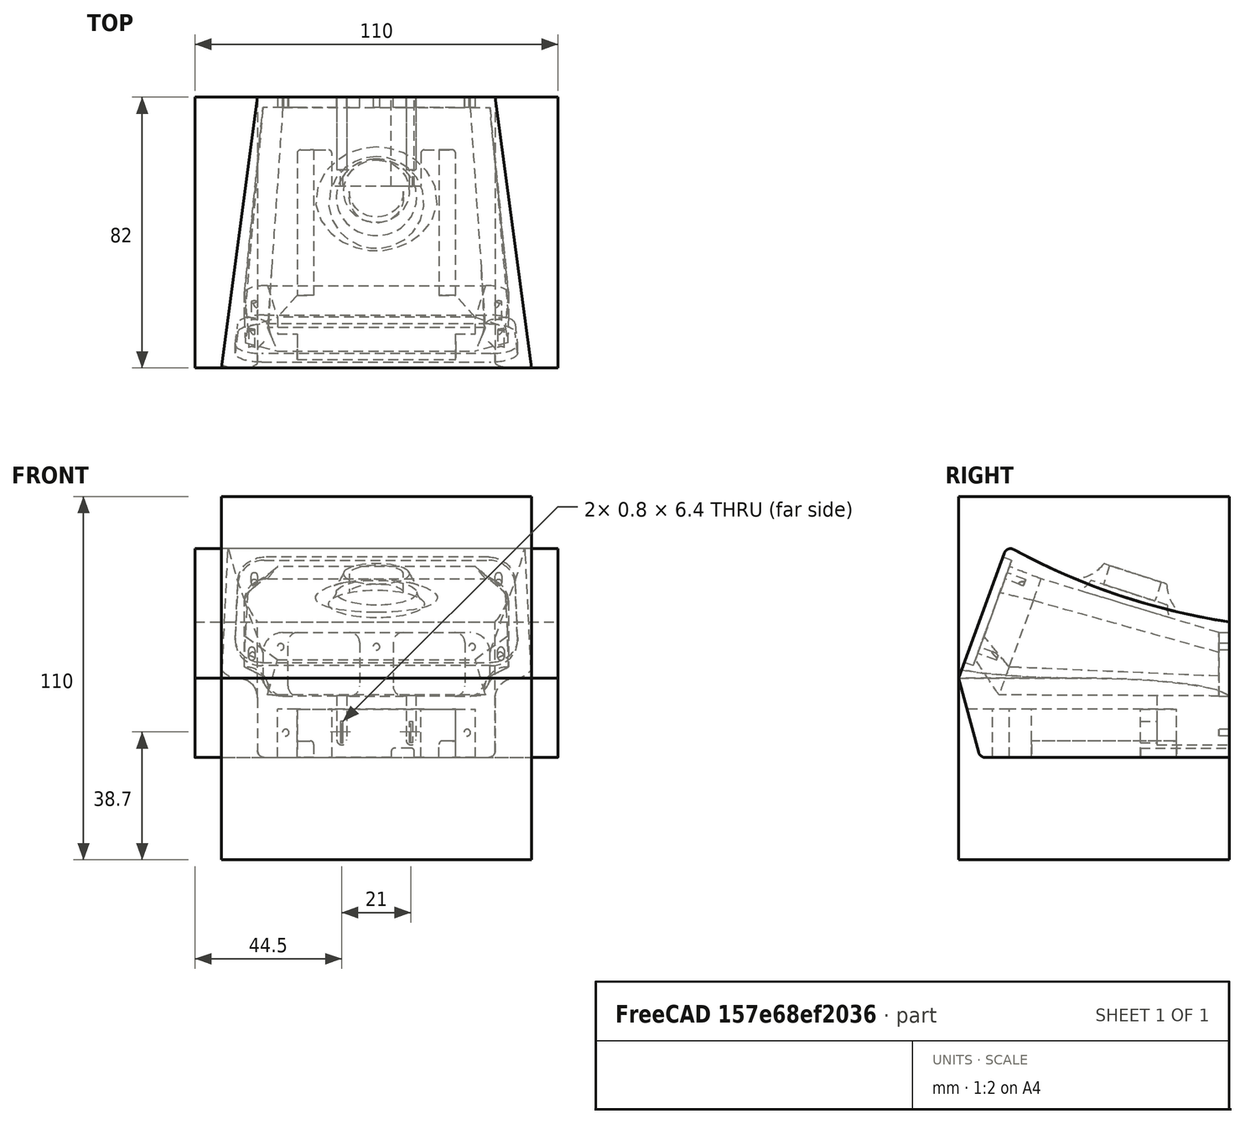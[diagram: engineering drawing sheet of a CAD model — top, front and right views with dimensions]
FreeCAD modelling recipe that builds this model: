
FCSTD DOCUMENT  (FreeCAD 0.19R24267 (Git))
Label: solder_station2
License: All rights reserved
LicenseURL: http://en.wikipedia.org/wiki/All_rights_reserved
objects: Sketcher::SketchObject×16, PartDesign::Pocket×7, PartDesign::Pad×4, PartDesign::Body×3, Spreadsheet::Sheet×1, Mesh::Feature×1, PartDesign::Boolean×1, PartDesign::SubtractiveLoft×1, PartDesign::Revolution×1, PartDesign::Groove×1, App::Part×1
note: 48 computed .brp shape members not serialized (recipe doc carries the construction recipe); baked Part::Feature solids carry a one-line shape summary decoded from their .brp

FEATURE [Sketcher::SketchObject] Sketch  label="RearSupport"
  AttachmentOffset = pos=(0,0,-37.8) rot=(0,0,1;0rad)
  FullyConstrained = true
  MapMode = 5
  Placement = pos=(0,37.8,8.4e-15) rot=(1,0,0;1.5708rad)
  Support = -> [XZ_Plane004]
  expr: .AttachmentOffset.Base.z = -<<param>>.mid_depth / 2 + <<param>>.wall
  expr: Constraints[37] = <<param>>.bottom_height
  expr: Constraints[38] = <<param>>.floor
  expr: Constraints[39] = <<param>>.rear_height - <<param>>.wall
  expr: Constraints[24] = 3
  expr: Constraints[47] = <<param>>.reart_screw_width2
  expr: Constraints[48] = <<param>>.rear_screw_width1
  expr: Constraints[52] = <<param>>.rear_screw_offset
  expr: Constraints[49] = <<param>>.screw_hole
  expr: Constraints[50] = <<param>>.rear_screw_height
  expr: Constraints[51] = <<param>>.rear_screw_height
  sketch-geometry (22):
    g0: LineSegment StartX=-23.8 StartY=13.8 StartZ=0 EndX=-8.1 EndY=13.8 EndZ=0
    g1: LineSegment StartX=26.8 StartY=10.8 StartZ=0 EndX=26.8 EndY=-2.4 EndZ=0
    g2: LineSegment StartX=23.8 StartY=-5.4 StartZ=0 EndX=8.1 EndY=-5.4 EndZ=0
    g3: LineSegment StartX=-26.8 StartY=-2.4 StartZ=0 EndX=-26.8 EndY=10.8 EndZ=0
    g4: LineSegment StartX=-5.1 StartY=10.8 StartZ=0 EndX=-5.1 EndY=-2.4 EndZ=0
    g5: LineSegment StartX=5.1 StartY=10.8 StartZ=0 EndX=5.1 EndY=-2.4 EndZ=0
    g6: LineSegment StartX=8.1 StartY=13.8 StartZ=0 EndX=23.8 EndY=13.8 EndZ=0
    g7: LineSegment StartX=-8.1 StartY=-5.4 StartZ=0 EndX=-23.8 EndY=-5.4 EndZ=0
    g8: ArcOfCircle CenterX=-8.1 CenterY=10.8 CenterZ=0 NormalX=0 NormalY=0 NormalZ=1 AngleXU=0 Radius=3 StartAngle=0 EndAngle=1.5708
    g9: ArcOfCircle CenterX=8.1 CenterY=10.8 CenterZ=0 NormalX=0 NormalY=0 NormalZ=1 AngleXU=0 Radius=3 StartAngle=1.5708 EndAngle=3.14159
    g10: ArcOfCircle CenterX=-8.1 CenterY=-2.4 CenterZ=0 NormalX=0 NormalY=0 NormalZ=1 AngleXU=0 Radius=3 StartAngle=4.71239 EndAngle=6.28319
    g11: ArcOfCircle CenterX=8.1 CenterY=-2.4 CenterZ=0 NormalX=0 NormalY=0 NormalZ=1 AngleXU=0 Radius=3 StartAngle=3.14159 EndAngle=4.71239
    g12: ArcOfCircle CenterX=-23.8 CenterY=10.8 CenterZ=0 NormalX=0 NormalY=0 NormalZ=1 AngleXU=0 Radius=3 StartAngle=1.5708 EndAngle=3.14159
    g13: ArcOfCircle CenterX=-23.8 CenterY=-2.4 CenterZ=0 NormalX=0 NormalY=0 NormalZ=1 AngleXU=0 Radius=3 StartAngle=3.14159 EndAngle=4.71239
    g14: ArcOfCircle CenterX=23.8 CenterY=10.8 CenterZ=0 NormalX=0 NormalY=0 NormalZ=1 AngleXU=0 Radius=3 StartAngle=0 EndAngle=1.5708
    g15: ArcOfCircle CenterX=23.8 CenterY=-2.4 CenterZ=0 NormalX=0 NormalY=0 NormalZ=1 AngleXU=0 Radius=3 StartAngle=4.71239 EndAngle=6.28319
    g16: Circle CenterX=0 CenterY=-24 CenterZ=0 NormalX=0 NormalY=0 NormalZ=1 AngleXU=0 Radius=3
    g17: Circle CenterX=0 CenterY=9.5 CenterZ=0 NormalX=0 NormalY=0 NormalZ=1 AngleXU=0 Radius=1
    g18: Circle CenterX=-29 CenterY=9.5 CenterZ=0 NormalX=0 NormalY=0 NormalZ=1 AngleXU=0 Radius=1
    g19: Circle CenterX=-27.5 CenterY=-16.5 CenterZ=0 NormalX=0 NormalY=0 NormalZ=1 AngleXU=0 Radius=1
    g20: Circle CenterX=27.5 CenterY=-16.5 CenterZ=0 NormalX=0 NormalY=0 NormalZ=1 AngleXU=0 Radius=1
    g21: Circle CenterX=29 CenterY=9.5 CenterZ=0 NormalX=0 NormalY=0 NormalZ=1 AngleXU=0 Radius=1
  constraints (53):
    c: Horizontal(g0)
    c: Horizontal(g2)
    c: Vertical(g1)
    c: Vertical(g3)
    c: Vertical(g4)
    c: Vertical(g5)
    c: Tangent(g0,g6)
    c: Tangent(g2,g7)
    c: Tangent(g0,g8) = 1.5708
    c: Tangent(g4,g8) = 1.5708
    c: Tangent(g5,g9) = -1.5708
    c: Tangent(g6,g9) = 1.5708
    c: Tangent(g7,g10) = 1.5708
    c: Tangent(g4,g10) = 1.5708
    c: Tangent(g5,g11) = -1.5708
    c: Tangent(g2,g11) = 1.5708
    c: Tangent(g0,g12) = 1.5708
    c: Tangent(g3,g12) = 1.5708
    c: Tangent(g3,g13) = 1.5708
    c: Tangent(g7,g13) = 1.5708
    c: Tangent(g6,g14) = 1.5708
    c: Tangent(g1,g14) = 1.5708
    c: Tangent(g1,g15) = 1.5708
    c: Tangent(g2,g15) = 1.5708
    c: Radius(g9) = 3
    c: Equal(g12,g13)
    c: Equal(g13,g10)
    c: Equal(g10,g8)
    c: Equal(g11,g15)
    c: Equal(g15,g14)
    c: Equal(g14,g9)
    c: DistanceX(g4,g-1) = 5.1
    c: DistanceX(g5,g1) = 21.7
    c: Symmetric(g4,g5,g-2)
    c: Equal(g7,g2)
    c: PointOnObject(g16,g-2)
    c: Radius(g16) = 3
    c: DistanceY(g16,g-1) = 24
    c: DistanceY(g16,g2) = 18.6
    c: DistanceY(g16,g6) = 37.8
    c: PointOnObject(g17,g-2)
    c: Equal(g21,g18)
    c: Equal(g18,g19)
    c: Equal(g19,g20)
    c: Equal(g18,g17)
    c: Symmetric(g20,g19,g-2)
    c: Symmetric(g18,g21,g-2)
    c: DistanceX(g19,g20) = 55
    c: DistanceX(g18,g21) = 58
    c: Diameter(g19) = 2
    c: DistanceY(g20,g21) = 26
    c: DistanceY(g20,g17) = 26
    c: DistanceY(g16,g19) = 7.5
FEATURE [Spreadsheet::Sheet] Spreadsheet  label="param"
  cells = A1=Body; B2=top_depth; C2(top_depth)=70; B3=mid_depth; C3(mid_depth)=82; D3=half is rear reference; B4=bottom_depth; C4(bottom_depth)=75; B6=bottom_width; C6(bottom_width)=72; B7=bottom_height; C7(bottom_height)=24; B8=bottom_angle; C8(bottom_angle)=15; B10=rear_width; C10(rear_width)=72; B11=rear_height; C11(rear_height)=41; B13=mid_width; C13(mid_width)=80; B14=mid_height; C14(mid_height)=50; B16=front_width1; C16(front_width1)=91; D16=@top; E16=not used; B17=front_width2; C17(front_width2)=94; D17=@mid; B18=front_height; C18(front_height)=63; B19=front_angle; C19(front_angle)=20; B21=wall; C21(wall)=3.2; B22=radius_big; C22(radius_big)=6; B23=radius_small; C23(radius_small)=2; B24=arch; C24(arch)=200; A26=Button; B27=button_offset; C27(button_offset)=10; B28=button_inside_dia; C28(button_inside_dia)=20; B29=button_outside_dia; C29(button_outside_dia)=40; B30=button_height; C30(button_height)=24; B31=button_extension; C31(button_extension)=8; B32=button_fillet; C32(button_fillet)=12; B33=button_angle; C33(button_angle)=-18; B34=button_hole; C34(button_hole)=16.4; B35=button_hole_center; C35(button_hole_center)=-0.5; A37=Battery Cuts; B38=batt_carveout; C38(batt_carveout)=14.6; B39=batt_rail; C39(batt_rail)=5; B40=batt_rail_length; C40(batt_rail_length)=44; A42=Terminals; B43=terminal_height; C43(terminal_height)=6.4; B44=terminal_thickness; C44(terminal_thickness)=0.8; B45=terminal_seperation; C45(terminal_seperation)=21; B46=terminal_offset; C46(terminal_offset)=4.5; B47=terminal_depth; C47(terminal_depth)=22; A49=Box Interior; B50=floor; C50(floor)=18.6; B51=rear_inside_width; C51(rear_inside_width)==C10 - C21; D51=calc; B52=rear_inside_height; C52(rear_inside_height)==C11 - C21; D52=calc; B53=mid_inside_width; C53(mid_inside_width)==C13; D53=calc; B54=mid_inside_height; C54(mid_inside_height)==C14 + 6; D54=calc; B55=front_inside_width1; C55(front_inside_width1)==C62 - C58 * 2; D55=calc; B56=front_inside_width2; C56(front_inside_width2)==C63 - C58 * 2; D56=calc; B57=front_inside_height; C57(front_inside_height)==C64 - C59 * 2; D57=calc; B58=front_width_lip_width; C58(front_width_lip_width)=3; B59=front_inside_lip_height; C59(front_inside_lip_height)=2; A61=Face; B62=face_width1; C62(face_width1)=84; B63=face_width2; C63(face_width2)=85.5; B64=face_height; C64(face_height)=34; B65=face_thickness; C65(face_thickness)=3; B66=face_radius; C66(face_radius)=8; B67=face_offset; C67(face_offset)=4; A69=Screws; B70=screw_hole; C70(screw_hole)=2; B72=front_screw_width1; C72(front_screw_width1)=74; B73=front_screw_width2; C73(front_screw_width2)=75.5; B74=front_screw_height; C74(front_screw_height)=24; B75=front_screw_offset; C75(front_screw_offset)=5; B77=rear_screw_width1; C77(rear_screw_width1)=58; B78=reart_screw_width2; C78(reart_screw_width2)=55; B79=rear_screw_height; C79(rear_screw_height)=26; B80=rear_screw_offset; C80(rear_screw_offset)=7.5
FEATURE [Sketcher::SketchObject] Sketch008  label="SketchButtonHole"
  AttachmentOffset = pos=(0,-0.5,24) rot=(1,0,0;-0.314159rad)
  FullyConstrained = true
  MapMode = 5
  Placement = pos=(0,-0.5,24) rot=(1,0,0;5.96903rad)
  Support = -> [XY_Plane004]
  expr: .AttachmentOffset.Base.z = <<param>>.button_height
  expr: Constraints[0] = <<param>>.button_hole
  expr: .AttachmentOffset.Base.y = <<param>>.button_hole_center
  expr: .AttachmentOffset.Rotation.Angle = <<param>>.button_angle
  expr: Constraints[2] = <<param>>.button_offset
  sketch-geometry (1):
    g0: Circle CenterX=0 CenterY=10 CenterZ=0 NormalX=0 NormalY=0 NormalZ=1 AngleXU=0 Radius=8.2
  constraints (3):
    c: Diameter(g0) = 16.4
    c: PointOnObject(g0,g-2)
    c: DistanceY(g-1,g0) = 10
FEATURE [Mesh::Feature] M18_soldering_case
  Placement = pos=(48,-41,-24) rot=(0,0.707107,0.707107;3.14159rad)
FEATURE [Sketcher::SketchObject] Sketch012  label="SketchSide"
  FullyConstrained = true
  MapMode = 5
  Placement = pos=(0,0,0) rot=(0.57735,0.57735,0.57735;2.0944rad)
  Support = -> [YZ_Plane002]
  expr: Constraints[24] = <<param>>.front_height - 0.01
  expr: Constraints[20] = 90 - <<param>>.bottom_angle
  expr: Constraints[19] = <<param>>.radius_small
  expr: Constraints[18] = <<param>>.bottom_height
  expr: Constraints[8] = <<param>>.arch
  expr: Constraints[6] = <<param>>.rear_height - <<param>>.bottom_height
  expr: Constraints[7] = <<param>>.radius_small
  expr: Constraints[21] = 90 - <<param>>.front_angle
  expr: Constraints[9] = <<param>>.mid_depth
  sketch-geometry (8):
    g0: LineSegment StartX=41 StartY=0 StartZ=0 EndX=41 EndY=17 EndZ=0
    g1: LineSegment StartX=-41 StartY=0 StartZ=0 EndX=-27.1994 EndY=37.9168 EndZ=0
    g2: ArcOfCircle CenterX=-25.32 CenterY=37.2327 CenterZ=0 NormalX=0 NormalY=0 NormalZ=1 AngleXU=0 Radius=2 StartAngle=1.07299 EndAngle=2.79253
    g3: ArcOfCircle CenterX=71.1341 CenterY=214.717 CenterZ=0 NormalX=0 NormalY=0 NormalZ=1 AngleXU=0 Radius=200 StartAngle=4.21459 EndAngle=4.56114
    g4: LineSegment StartX=-41 StartY=0 StartZ=0 EndX=-34.9664 EndY=-22.5176 EndZ=0
    g5: LineSegment StartX=-33.0346 StartY=-24 StartZ=0 EndX=41 EndY=-24 EndZ=0
    g6: LineSegment StartX=41 StartY=-24 StartZ=0 EndX=41 EndY=0 EndZ=0
    g7: ArcOfCircle CenterX=-33.0346 CenterY=-22 CenterZ=0 NormalX=0 NormalY=0 NormalZ=1 AngleXU=0 Radius=2 StartAngle=3.40339 EndAngle=4.71239
  constraints (25):
    c: PointOnObject(g1,g-1)
    c: Vertical(g0)
    c: Coincident(g2,g1)
    c: Coincident(g3,g0)
    c: Tangent(g3,g2) = 1.5708
    c: Symmetric(g1,g0,g-2)
    c: DistanceY(g0,g0) = 17
    c: Radius(g2) = 2
    c: Radius(g3) = 200
    c: DistanceX(g1,g0) = 82
    c: Tangent(g2,g1)
    c: Horizontal(g5)
    c: Coincident(g6,g5)
    c: Vertical(g6)
    c: Coincident(g7,g4)
    c: Coincident(g7,g5)
    c: Tangent(g7,g5)
    c: Tangent(g7,g4)
    c: DistanceY(g5,g-1) = 24
    c: Radius(g7) = 2
    c: Angle(g4,g-1) = 1.309
    c: Angle(g-1,g1) = 1.22173
    c: Coincident(g4,g1)
    c: Coincident(g6,g0)
    c: DistanceY(g5,g2) = 62.99
FEATURE [PartDesign::Pad] Pad  label="PadSide"
  Direction = (1,1,1)
  Length = 110
  Length2 = 100
  Midplane = true
  Placement = pos=(0,0,0) rot=(0.57735,0.57735,0.57735;2.0944rad)
  Profile = -> Sketch012
  Type = 0
FEATURE [PartDesign::Body] Body001  label="BodySide"
  Group = -> [Sketch012,Pad]
  Origin = -> Origin002
  Tip = -> Pad
FEATURE [Sketcher::SketchObject] Sketch013  label="SketchTop"
  FullyConstrained = true
  MapMode = 5
  Support = -> [XY_Plane003]
  expr: Constraints[4] = <<param>>.front_width2
  expr: Constraints[6] = <<param>>.rear_width
  expr: Constraints[8] = <<param>>.mid_depth
  expr: Constraints[9] = <<param>>.mid_depth / 2
  sketch-geometry (4):
    g0: LineSegment StartX=36 StartY=41 StartZ=0 EndX=-36 EndY=41 EndZ=0
    g1: LineSegment StartX=-36 StartY=41 StartZ=0 EndX=-47 EndY=-41 EndZ=0
    g2: LineSegment StartX=-47 StartY=-41 StartZ=0 EndX=47 EndY=-41 EndZ=0
    g3: LineSegment StartX=47 StartY=-41 StartZ=0 EndX=36 EndY=41 EndZ=0
  constraints (10):
    c: Coincident(g0,g1)
    c: Coincident(g1,g2)
    c: Coincident(g2,g3)
    c: Coincident(g3,g0)
    c: DistanceX(g1,g2) = 94
    c: Symmetric(g2,g1,g-2)
    c: DistanceX(g0,g0) = 72
    c: Symmetric(g0,g0,g-2)
    c: DistanceY(g2,g0) = 82
    c: DistanceY(g2,g-1) = 41
FEATURE [PartDesign::Pad] Pad001  label="PadTop"
  Direction = (1,1,1)
  Length = 110
  Length2 = 100
  Midplane = true
  Profile = -> Sketch013
  Type = 0
FEATURE [PartDesign::Body] Body002  label="BodyTop"
  Group = -> [Sketch013,Pad001]
  Origin = -> Origin003
  Tip = -> Pad001
FEATURE [Sketcher::SketchObject] Sketch017  label="SketchFront"
  FullyConstrained = true
  MapMode = 5
  Placement = pos=(0,0,0) rot=(1,0,0;1.5708rad)
  Support = -> [XZ_Plane004]
  expr: Constraints[37] = <<param>>.front_height + 2
  expr: Constraints[35] = <<param>>.front_width2
  expr: Constraints[34] = <<param>>.front_width1
  expr: Constraints[33] = <<param>>.bottom_width
  expr: Constraints[38] = <<param>>.bottom_height
  expr: Constraints[29] = <<param>>.radius_big
  expr: Constraints[28] = <<param>>.radius_small
  sketch-geometry (12):
    g0: LineSegment StartX=-34 StartY=-24 StartZ=0 EndX=34 EndY=-24 EndZ=0
    g1: LineSegment StartX=36 StartY=-22 StartZ=0 EndX=36 EndY=-6 EndZ=0
    g2: LineSegment StartX=-36 StartY=-22 StartZ=0 EndX=-36 EndY=-6 EndZ=0
    g3: ArcOfCircle CenterX=-42 CenterY=-6 CenterZ=0 NormalX=0 NormalY=0 NormalZ=1 AngleXU=0 Radius=6 StartAngle=6.28319 EndAngle=7.85398
    g4: ArcOfCircle CenterX=42 CenterY=-6 CenterZ=0 NormalX=0 NormalY=0 NormalZ=1 AngleXU=0 Radius=6 StartAngle=1.5708 EndAngle=3.14159
    g5: ArcOfCircle CenterX=42 CenterY=6 CenterZ=0 NormalX=0 NormalY=0 NormalZ=1 AngleXU=0 Radius=6 StartAngle=4.71239 EndAngle=5.6975
    g6: ArcOfCircle CenterX=-42 CenterY=6 CenterZ=0 NormalX=0 NormalY=0 NormalZ=1 AngleXU=0 Radius=6 StartAngle=3.72728 EndAngle=4.71239
    g7: LineSegment StartX=47 StartY=2.68336 StartZ=0 EndX=45.5 EndY=41 EndZ=0
    g8: LineSegment StartX=-45.5 StartY=41 StartZ=0 EndX=45.5 EndY=41 EndZ=0
    g9: ArcOfCircle CenterX=34 CenterY=-22 CenterZ=0 NormalX=0 NormalY=0 NormalZ=1 AngleXU=0 Radius=2 StartAngle=4.71238 EndAngle=6.28318
    g10: ArcOfCircle CenterX=-34 CenterY=-22 CenterZ=0 NormalX=0 NormalY=0 NormalZ=1 AngleXU=0 Radius=2 StartAngle=3.14159 EndAngle=4.71239
    g11: LineSegment StartX=-45.5 StartY=41 StartZ=0 EndX=-47 EndY=2.68336 EndZ=0
  constraints (39):
    c: Coincident(g8,g11)
    c: Coincident(g8,g7)
    c: Coincident(g11,g6)
    c: Coincident(g5,g7)
    c: Coincident(g0,g9)
    c: Coincident(g9,g1)
    c: Coincident(g0,g10)
    c: Coincident(g2,g10)
    c: Coincident(g2,g3)
    c: Coincident(g4,g1)
    c: Coincident(g4,g5)
    c: Coincident(g6,g3)
    c: Vertical(g1)
    c: Vertical(g2)
    c: PointOnObject(g4,g-1)
    c: Symmetric(g4,g3,g-2)
    c: Symmetric(g0,g0,g-2)
    c: Symmetric(g7,g8,g-2)
    c: Tangent(g9,g0)
    c: Tangent(g9,g1)
    c: Tangent(g10,g0)
    c: Tangent(g10,g2)
    c: Tangent(g3,g2)
    c: Tangent(g4,g1)
    c: Equal(g3,g6)
    c: Equal(g6,g4)
    c: Equal(g4,g5)
    c: Equal(g9,g10)
    c: Radius(g9) = 2
    c: Radius(g4) = 6
    c: Tangent(g4,g5)
    c: Tangent(g3,g6)
    c: Vertical(g4,g4)
    c: DistanceX(g2,g1) = 72
    c: DistanceX(g8,g8) = 91
    c: DistanceX(g6,g5) = 94
    c: Equal(g11,g7)
    c: DistanceY(g0,g7) = 65
    c: DistanceY(g0,g4) = 24
FEATURE [PartDesign::Pad] Pad003  label="PadFront"
  Direction = (1,1,1)
  Length = 110
  Length2 = 100
  Midplane = true
  Placement = pos=(0,0,0) rot=(1,0,0;1.5708rad)
  Profile = -> Sketch017
  Type = 0
FEATURE [PartDesign::Boolean] Boolean
  BaseFeature = -> Pad003
  Group = -> [Body002,Body001]
  Refine = true
  Type = 2
FEATURE [Sketcher::SketchObject] Sketch018  label="SketchBat1"
  AttachmentOffset = pos=(0,0,-24) rot=(0,0,1;0rad)
  FullyConstrained = true
  MapMode = 5
  Placement = pos=(0,0,-24) rot=(0,0,1;0rad)
  Support = -> [XY_Plane004]
  expr: .AttachmentOffset.Base.z = -<<param>>.bottom_height
  expr: Constraints[64] = <<param>>.mid_depth / 2
  sketch-geometry (21):
    g0: LineSegment StartX=-24 StartY=-40.7082 StartZ=0 EndX=24 EndY=-40.7082 EndZ=0
    g1: LineSegment StartX=24 StartY=-40.7082 StartZ=0 EndX=24 EndY=-30.7082 EndZ=0
    g2: LineSegment StartX=24 StartY=-30.7082 StartZ=0 EndX=30 EndY=-30.7082 EndZ=0
    g3: LineSegment StartX=30 StartY=-30.7082 StartZ=0 EndX=30 EndY=-25.7082 EndZ=0
    g4: LineSegment StartX=30 StartY=-25.7082 StartZ=0 EndX=24 EndY=-19 EndZ=0
    g5: LineSegment StartX=24 StartY=-19 StartZ=0 EndX=24 EndY=24 EndZ=0
    g6: LineSegment StartX=13.5 StartY=24 StartZ=0 EndX=13.5 EndY=14 EndZ=0
    g7: LineSegment StartX=13.5 StartY=14 StartZ=0 EndX=-13.5 EndY=14 EndZ=0
    g8: LineSegment StartX=-13.5 StartY=14 StartZ=0 EndX=-13.5 EndY=24 EndZ=0
    g9: LineSegment StartX=-24 StartY=24 StartZ=0 EndX=-24 EndY=-19 EndZ=0
    g10: LineSegment StartX=-24 StartY=-19 StartZ=0 EndX=-30 EndY=-25.7082 EndZ=0
    g11: LineSegment StartX=-30 StartY=-25.7082 StartZ=0 EndX=-30 EndY=-30.7082 EndZ=0
    g12: LineSegment StartX=-30 StartY=-30.7082 StartZ=0 EndX=-24 EndY=-30.7082 EndZ=0
    g13: LineSegment StartX=-24 StartY=-30.7082 StartZ=0 EndX=-24 EndY=-40.7082 EndZ=0
    g14: Circle CenterX=0 CenterY=41 CenterZ=0 NormalX=0 NormalY=0 NormalZ=1 AngleXU=0 Radius=4
    g15: ArcOfCircle CenterX=-14.5 CenterY=24 CenterZ=0 NormalX=0 NormalY=0 NormalZ=1 AngleXU=0 Radius=1 StartAngle=6.28319 EndAngle=7.85398
    g16: LineSegment StartX=-23 StartY=25 StartZ=0 EndX=-14.5 EndY=25 EndZ=0
    g17: LineSegment StartX=14.5 StartY=25 StartZ=0 EndX=23 EndY=25 EndZ=0
    g18: ArcOfCircle CenterX=-23 CenterY=24 CenterZ=0 NormalX=0 NormalY=0 NormalZ=1 AngleXU=0 Radius=1 StartAngle=1.5708 EndAngle=3.14159
    g19: ArcOfCircle CenterX=14.5 CenterY=24 CenterZ=0 NormalX=0 NormalY=0 NormalZ=1 AngleXU=0 Radius=1 StartAngle=1.5708 EndAngle=3.14159
    g20: ArcOfCircle CenterX=23 CenterY=24 CenterZ=0 NormalX=0 NormalY=0 NormalZ=1 AngleXU=0 Radius=1 StartAngle=6.28319 EndAngle=7.85398
  constraints (65):
    c: Horizontal(g0)
    c: Coincident(g1,g0)
    c: Vertical(g1)
    c: Coincident(g2,g1)
    c: Horizontal(g2)
    c: Coincident(g3,g2)
    c: Coincident(g3,g4)
    c: Vertical(g5)
    c: Coincident(g6,g7)
    c: Coincident(g7,g8)
    c: Vertical(g8)
    c: Vertical(g9)
    c: Coincident(g10,g11)
    c: Vertical(g11)
    c: Coincident(g11,g12)
    c: Horizontal(g12)
    c: Coincident(g12,g13)
    c: Equal(g6,g8)
    c: Equal(g5,g9)
    c: Equal(g4,g10)
    c: Equal(g3,g11)
    c: Equal(g12,g2)
    c: Equal(g1,g13)
    c: Coincident(g13,g0)
    c: Vertical(g13)
    c: DistanceX(g7,g7) = 27
    c: Symmetric(g7,g6,g-2)
    c: Distance(g4) = 9
    c: Vertical(g3)
    c: DistanceY(g3,g3) = 5
    c: DistanceX(g2,g2) = 6
    c: DistanceY(g1,g1) = 10
    c: DistanceX(g0,g0) = 48
    c: PointOnObject(g14,g-2)
    c: Coincident(g9,g10)
    c: Coincident(g5,g4)
    c: Coincident(g15,g8)
    c: Coincident(g16,g15)
    c: Tangent(g15,g8)
    c: Horizontal(g16)
    c: Horizontal(g17)
    c: DistanceX(g9,g5) = 48
    c: Symmetric(g4,g9,g-2)
    c: Equal(g16,g17)
    c: Coincident(g18,g9)
    c: Coincident(g18,g16)
    c: Equal(g18,g15)
    c: Tangent(g18,g16)
    c: Tangent(g18,g9)
    c: DistanceY(g6,g17) = 11
    c: Vertical(g6)
    c: Coincident(g19,g6)
    c: Coincident(g19,g17)
    c: Coincident(g20,g17)
    c: Coincident(g20,g5)
    c: Tangent(g20,g17)
    c: Tangent(g20,g5)
    c: Tangent(g19,g6)
    c: Tangent(g19,g17)
    c: Equal(g15,g19)
    c: Radius(g19) = 1
    c: Radius(g14) = 4
    c: DistanceY(g15,g14) = 16
    c: DistanceY(g9,g16) = 44
    c: DistanceY(g-1,g14) = 41
FEATURE [PartDesign::Pocket] Pocket  label="PocketBatt"
  BaseFeature = -> Boolean
  Length = 14.6
  Length2 = 100
  Profile = -> Sketch018
  Reversed = true
  Type = 0
  expr: Length = Spreadsheet.batt_carveout
FEATURE [Sketcher::SketchObject] Sketch019  label="SketchBat2"
  AttachmentOffset = pos=(0,0,-25) rot=(0,0,1;0rad)
  FullyConstrained = true
  MapMode = 5
  Placement = pos=(0,25,5.6e-15) rot=(1,0,0;1.5708rad)
  Support = -> [XZ_Plane004]
  expr: Constraints[28] = 48.01mm
  expr: .AttachmentOffset.Base.z = -<<param>>.mid_depth / 2 + 16
  expr: Constraints[26] = <<param>>.bottom_height
  expr: Constraints[29] = <<param>>.batt_rail
  expr: Constraints[27] = <<param>>.batt_rail
  sketch-geometry (10):
    g0: LineSegment StartX=-24.005 StartY=-19 StartZ=0 EndX=-20.005 EndY=-19 EndZ=0
    g1: LineSegment StartX=-19.005 StartY=-24 StartZ=0 EndX=-24.005 EndY=-24 EndZ=0
    g2: LineSegment StartX=-24.005 StartY=-24 StartZ=0 EndX=-24.005 EndY=-19 EndZ=0
    g3: LineSegment StartX=24.005 StartY=-19 StartZ=0 EndX=20.005 EndY=-19 EndZ=0
    g4: LineSegment StartX=19.005 StartY=-24 StartZ=0 EndX=24.005 EndY=-24 EndZ=0
    g5: LineSegment StartX=24.005 StartY=-24 StartZ=0 EndX=24.005 EndY=-19 EndZ=0
    g6: LineSegment StartX=-19.005 StartY=-20 StartZ=0 EndX=-19.005 EndY=-24 EndZ=0
    g7: ArcOfCircle CenterX=20.005 CenterY=-20 CenterZ=0 NormalX=0 NormalY=0 NormalZ=1 AngleXU=0 Radius=1 StartAngle=1.5708 EndAngle=3.14158
    g8: LineSegment StartX=19.005 StartY=-24 StartZ=0 EndX=19.005 EndY=-20 EndZ=0
    g9: ArcOfCircle CenterX=-20.005 CenterY=-20 CenterZ=0 NormalX=0 NormalY=0 NormalZ=1 AngleXU=0 Radius=1 StartAngle=6.28317 EndAngle=7.85398
  constraints (30):
    c: Coincident(g1,g2)
    c: Coincident(g2,g0)
    c: Horizontal(g0)
    c: Horizontal(g1)
    c: Vertical(g2)
    c: Coincident(g4,g5)
    c: Coincident(g5,g3)
    c: Horizontal(g3)
    c: Horizontal(g4)
    c: Vertical(g5)
    c: Coincident(g6,g1)
    c: Vertical(g6)
    c: Equal(g1,g4)
    c: Tangent(g3,g7) = -1.5708
    c: Coincident(g8,g4)
    c: Vertical(g8)
    c: Coincident(g7,g8)
    c: Coincident(g9,g0)
    c: Coincident(g9,g6)
    c: Equal(g6,g8)
    c: Tangent(g7,g8)
    c: Tangent(g9,g6)
    c: Tangent(g9,g0)
    c: Equal(g9,g7)
    c: Radius(g9) = 1
    c: Symmetric(g1,g4,g-2)
    c: DistanceY(g1,g-1) = 24
    c: DistanceY(g4,g3) = 5
    c: DistanceX(g1,g4) = 48.01
    c: DistanceX(g4,g4) = 5
FEATURE [PartDesign::Pad] Pad004  label="PadRail"
  BaseFeature = -> Pocket
  Direction = (1,1,1)
  Length = 44
  Length2 = 100
  Profile = -> Sketch019
  Type = 0
  expr: Length = <<param>>.batt_rail_length
FEATURE [Sketcher::SketchObject] Sketch021  label="SketchButton"
  AttachmentOffset = pos=(10,24,0) rot=(0,0,1;-0.314159rad)
  FullyConstrained = true
  MapMode = 5
  Placement = pos=(-3.1e-15,10,24) rot=(-0.506732,-0.697457,-0.506732;4.35963rad)
  Support = -> [YZ_Plane004]
  expr: .AttachmentOffset.Base.x = <<param>>.button_offset
  expr: .AttachmentOffset.Rotation.Angle = <<param>>.button_angle
  expr: .AttachmentOffset.Base.y = <<param>>.button_height
  expr: Constraints[11] = <<param>>.button_fillet
  expr: Constraints[10] = <<param>>.button_outside_dia / 2
  expr: Constraints[9] = <<param>>.button_inside_dia / 2
  expr: Constraints[8] = <<param>>.button_extension
  sketch-geometry (4):
    g0: ArcOfCircle CenterX=21.34 CenterY=11.925 CenterZ=0 NormalX=0 NormalY=0 NormalZ=1 AngleXU=0 Radius=12 StartAngle=3.4748 EndAngle=4.60049
    g1: LineSegment StartX=0 StartY=2.13e-14 StartZ=0 EndX=0 EndY=8 EndZ=0
    g2: LineSegment StartX=0 StartY=8 StartZ=0 EndX=10 EndY=8 EndZ=0
    g3: LineSegment StartX=0 StartY=2.13e-14 StartZ=0 EndX=20 EndY=2.13e-14 EndZ=0
  constraints (12):
    c: Coincident(g1,g-1)
    c: PointOnObject(g1,g-2)
    c: Coincident(g2,g1)
    c: Coincident(g2,g0)
    c: Horizontal(g2)
    c: Coincident(g3,g1)
    c: Coincident(g3,g0)
    c: Horizontal(g3)
    c: DistanceY(g1,g1) = 8
    c: DistanceX(g2,g2) = 10
    c: DistanceX(g3,g3) = 20
    c: Radius(g0) = 12
FEATURE [Sketcher::SketchObject] Sketch022  label="SketchRearInside"
  AttachmentOffset = pos=(0,0,-37.8) rot=(0,0,1;0rad)
  FullyConstrained = true
  MapMode = 5
  Placement = pos=(0,37.8,8.4e-15) rot=(1,0,0;1.5708rad)
  Support = -> [XZ_Plane004]
  expr: Constraints[12] = <<param>>.radius_big
  expr: Constraints[18] = <<param>>.rear_inside_width
  expr: .AttachmentOffset.Base.z = -<<param>>.mid_depth / 2 + <<param>>.wall
  expr: Constraints[27] = <<param>>.rear_inside_height
  expr: Constraints[26] = <<param>>.bottom_height
  expr: Constraints[29] = <<param>>.floor
  sketch-geometry (9):
    g0: LineSegment StartX=-34.4 StartY=7.80002 StartZ=0 EndX=-34.4 EndY=0.600003 EndZ=0
    g1: LineSegment StartX=-28.4 StartY=-5.4 StartZ=0 EndX=28.4 EndY=-5.4 EndZ=0
    g2: LineSegment StartX=34.4 StartY=0.600003 StartZ=0 EndX=34.4 EndY=7.80002 EndZ=0
    g3: LineSegment StartX=-28.4 StartY=13.8 StartZ=0 EndX=28.4 EndY=13.8 EndZ=0
    g4: ArcOfCircle CenterX=28.4 CenterY=7.8 CenterZ=0 NormalX=0 NormalY=0 NormalZ=1 AngleXU=0 Radius=6 StartAngle=3.92565e-06 EndAngle=1.5708
    g5: ArcOfCircle CenterX=28.4 CenterY=0.6 CenterZ=0 NormalX=0 NormalY=0 NormalZ=1 AngleXU=0 Radius=6 StartAngle=4.71239 EndAngle=6.28319
    g6: ArcOfCircle CenterX=-28.4 CenterY=7.8 CenterZ=0 NormalX=0 NormalY=0 NormalZ=1 AngleXU=0 Radius=6 StartAngle=1.5708 EndAngle=3.14159
    g7: ArcOfCircle CenterX=-28.4 CenterY=0.6 CenterZ=0 NormalX=0 NormalY=0 NormalZ=1 AngleXU=0 Radius=6 StartAngle=3.14159 EndAngle=4.71239
    g8: Circle CenterX=0 CenterY=-24 CenterZ=0 NormalX=0 NormalY=0 NormalZ=1 AngleXU=0 Radius=3
  constraints (30):
    c: Vertical(g0)
    c: Horizontal(g1)
    c: Vertical(g2)
    c: Horizontal(g3)
    c: Equal(g3,g1)
    c: Equal(g0,g2)
    c: Coincident(g4,g3)
    c: Coincident(g4,g2)
    c: Coincident(g5,g2)
    c: Coincident(g5,g1)
    c: Coincident(g6,g0)
    c: Coincident(g6,g3)
    c: Radius(g6) = 6
    c: Equal(g6,g4)
    c: Equal(g4,g5)
    c: Coincident(g7,g1)
    c: Coincident(g7,g0)
    c: Equal(g5,g7)
    c: DistanceX(g0,g2) = 68.8
    c: Symmetric(g0,g2,g-2)
    c: Tangent(g4,g2)
    c: Tangent(g4,g3)
    c: Tangent(g5,g2)
    c: Tangent(g5,g1)
    c: Tangent(g6,g3)
    c: PointOnObject(g8,g-2)
    c: DistanceY(g8,g-1) = 24
    c: DistanceY(g8,g3) = 37.8
    c: Radius(g8) = 3
    c: DistanceY(g8,g1) = 18.6
FEATURE [Sketcher::SketchObject] Sketch023  label="SketchFrontInside"
  AttachmentOffset = pos=(0,0,38) rot=(1,0,0;-0.349066rad)
  FullyConstrained = true
  MapMode = 5
  Placement = pos=(0,-38,-8.4e-15) rot=(-1,0,0;5.06145rad)
  Support = -> [XZ_Plane004]
  expr: Constraints[1] = <<param>>.front_inside_width1
  expr: .AttachmentOffset.Base.z = <<param>>.mid_depth / 2 - <<param>>.face_thickness
  expr: Constraints[2] = <<param>>.front_inside_height
  expr: .AttachmentOffset.Rotation.Angle = -<<param>>.front_angle
  expr: Constraints[21] = <<param>>.face_offset + <<param>>.front_inside_lip_height
  expr: Constraints[20] = <<param>>.front_inside_width2 / 2
  expr: Constraints[19] = <<param>>.front_inside_width2
  sketch-geometry (8):
    g0: LineSegment StartX=-30 StartY=6 StartZ=0 EndX=30 EndY=6 EndZ=0
    g1: LineSegment StartX=30 StartY=36 StartZ=0 EndX=-30 EndY=36 EndZ=0
    g2: LineSegment StartX=-39 StartY=27.5605 StartZ=0 EndX=-39.75 EndY=13.5605 EndZ=0
    g3: LineSegment StartX=-39 StartY=27.5605 StartZ=0 EndX=-30 EndY=36 EndZ=0
    g4: LineSegment StartX=30 StartY=36 StartZ=0 EndX=39 EndY=27.5605 EndZ=0
    g5: LineSegment StartX=39.75 StartY=13.5605 StartZ=0 EndX=30 EndY=6 EndZ=0
    g6: LineSegment StartX=-39.75 StartY=13.5605 StartZ=0 EndX=-30 EndY=6 EndZ=0
    g7: LineSegment StartX=39 StartY=27.5605 StartZ=0 EndX=39.75 EndY=13.5605 EndZ=0
  constraints (22):
    c: Symmetric(g0,g0,g-2)
    c: DistanceX(g2,g4) = 78
    c: DistanceY(g0,g1) = 30
    c: Symmetric(g1,g1,g-2)
    c: Coincident(g3,g2)
    c: Coincident(g3,g1)
    c: Coincident(g4,g1)
    c: Coincident(g5,g0)
    c: Coincident(g6,g2)
    c: Coincident(g6,g0)
    c: Equal(g3,g6)
    c: Equal(g6,g5)
    c: Equal(g5,g4)
    c: Coincident(g7,g4)
    c: Coincident(g7,g5)
    c: DistanceY(g7,g7) = 14
    c: Equal(g7,g2)
    c: Equal(g1,g0)
    c: DistanceX(g1,g1) = 60
    c: DistanceX(g2,g5) = 79.5
    c: DistanceX(g2,g-1) = 39.75
    c: DistanceY(g-1,g0) = 6
FEATURE [Sketcher::SketchObject] Sketch024  label="SketchFace"
  AttachmentOffset = pos=(0,0,38) rot=(1,0,0;-0.349066rad)
  FullyConstrained = true
  MapMode = 5
  Placement = pos=(0,-38,-8.4e-15) rot=(-1,0,0;5.06145rad)
  Support = -> [XZ_Plane004]
  expr: Constraints[23] = <<param>>.face_width2
  expr: .AttachmentOffset.Base.z = <<param>>.mid_depth / 2 - <<param>>.face_thickness
  expr: Constraints[13] = <<param>>.face_radius
  expr: Constraints[22] = <<param>>.face_width1
  expr: .AttachmentOffset.Rotation.Angle = -<<param>>.front_angle
  expr: Constraints[24] = <<param>>.face_offset
  expr: Constraints[25] = <<param>>.face_height
  sketch-geometry (8):
    g0: LineSegment StartX=-34.0069 StartY=38 StartZ=0 EndX=34.007 EndY=38 EndZ=0
    g1: LineSegment StartX=42 StartY=30.333 StartZ=0 EndX=42.75 EndY=12.333 EndZ=0
    g2: LineSegment StartX=34.7569 StartY=4 StartZ=0 EndX=-34.7569 EndY=4 EndZ=0
    g3: LineSegment StartX=-42.75 StartY=12.3331 StartZ=0 EndX=-42 EndY=30.3331 EndZ=0
    g4: ArcOfCircle CenterX=34.007 CenterY=30 CenterZ=0 NormalX=0 NormalY=0 NormalZ=1 AngleXU=0 Radius=8 StartAngle=0.0416407 EndAngle=1.5708
    g5: ArcOfCircle CenterX=34.7569 CenterY=12 CenterZ=0 NormalX=0 NormalY=0 NormalZ=1 AngleXU=0 Radius=8 StartAngle=4.71239 EndAngle=6.32483
    g6: ArcOfCircle CenterX=-34.0069 CenterY=30 CenterZ=0 NormalX=0 NormalY=0 NormalZ=1 AngleXU=0 Radius=8 StartAngle=1.5708 EndAngle=3.09995
    g7: ArcOfCircle CenterX=-34.7569 CenterY=12 CenterZ=0 NormalX=0 NormalY=0 NormalZ=1 AngleXU=0 Radius=8 StartAngle=3.09995 EndAngle=4.71239
  constraints (27):
    c: Horizontal(g0)
    c: Coincident(g4,g0)
    c: Coincident(g4,g1)
    c: Coincident(g5,g1)
    c: Coincident(g5,g2)
    c: Coincident(g6,g0)
    c: Coincident(g6,g3)
    c: Coincident(g7,g3)
    c: Coincident(g7,g2)
    c: Equal(g1,g3)
    c: Equal(g4,g6)
    c: Equal(g6,g7)
    c: Equal(g7,g5)
    c: Radius(g4) = 8
    c: Tangent(g6,g3)
    c: Tangent(g7,g3)
    c: Tangent(g7,g2)
    c: Tangent(g6,g0)
    c: Tangent(g4,g0)
    c: Tangent(g4,g1)
    c: Tangent(g5,g1)
    c: Tangent(g5,g2)
    c: DistanceX(g3,g1) = 84
    c: DistanceX(g3,g1) = 85.5
    c: DistanceY(g-1,g2) = 4
    c: DistanceY(g2,g0) = 34
    c: Symmetric(g2,g2,g-2)
FEATURE [PartDesign::Pocket] Pocket002  label="PocketRear"
  BaseFeature = -> Pad004
  Length = 4
  Length2 = 100
  Profile = -> Sketch
  Type = 0
FEATURE [Sketcher::SketchObject] Sketch025  label="SketchMidInside"
  AttachmentOffset = pos=(0,0,27) rot=(1,0,0;-0.349066rad)
  FullyConstrained = true
  MapMode = 5
  Placement = pos=(0,-27,-6e-15) rot=(-1,0,0;5.06145rad)
  Support = -> [XZ_Plane004]
  expr: Constraints[18] = <<param>>.mid_inside_height
  expr: .AttachmentOffset.Rotation.Angle = -<<param>>.front_angle
  expr: Constraints[12] = Spreadsheet.mid_inside_width
  expr: .AttachmentOffset.Base.z = <<param>>.mid_depth / 2 - 14
  expr: Constraints[11] = <<param>>.floor
  expr: Constraints[10] = <<param>>.radius_big + 1
  expr: Constraints[4] = <<param>>.bottom_height
  sketch-geometry (9):
    g0: LineSegment StartX=-33 StartY=32 StartZ=0 EndX=33 EndY=32 EndZ=0
    g1: LineSegment StartX=40 StartY=25 StartZ=0 EndX=40 EndY=3.59392 EndZ=0
    g2: LineSegment StartX=33 StartY=-5.4 StartZ=0 EndX=-33 EndY=-5.4 EndZ=0
    g3: LineSegment StartX=-40 StartY=3.59392 StartZ=0 EndX=-40 EndY=25 EndZ=0
    g4: Circle CenterX=0 CenterY=-24 CenterZ=0 NormalX=0 NormalY=0 NormalZ=1 AngleXU=0 Radius=3
    g5: ArcOfCircle CenterX=-33 CenterY=25 CenterZ=0 NormalX=0 NormalY=0 NormalZ=1 AngleXU=0 Radius=7 StartAngle=1.5708 EndAngle=3.14159
    g6: ArcOfCircle CenterX=33 CenterY=25 CenterZ=0 NormalX=0 NormalY=0 NormalZ=1 AngleXU=0 Radius=7 StartAngle=2e-16 EndAngle=1.5708
    g7: ArcOfCircle CenterX=39.7082 CenterY=-3.4 CenterZ=0 NormalX=0 NormalY=0 NormalZ=1 AngleXU=0 Radius=7 StartAngle=1.5291 EndAngle=3.43134
    g8: ArcOfCircle CenterX=-39.7082 CenterY=-3.4 CenterZ=0 NormalX=0 NormalY=0 NormalZ=1 AngleXU=0 Radius=7 StartAngle=5.99343 EndAngle=7.89568
  constraints (25):
    c: Vertical(g1)
    c: Vertical(g3)
    c: PointOnObject(g4,g-2)
    c: Radius(g4) = 3
    c: DistanceY(g4,g-1) = 24
    c: Tangent(g3,g5) = 1.5708
    c: Tangent(g0,g5) = 1.5708
    c: Tangent(g0,g6) = 1.5708
    c: Tangent(g1,g6) = 1.5708
    c: Equal(g6,g5)
    c: Radius(g6) = 7
    c: DistanceY(g4,g2) = 18.6
    c: DistanceX(g3,g1) = 80
    c: Symmetric(g2,g2,g-2)
    c: Coincident(g7,g2)
    c: Coincident(g7,g1)
    c: Coincident(g8,g3)
    c: Coincident(g8,g2)
    c: DistanceY(g4,g0) = 56
    c: DistanceY(g2,g7) = 2
    c: Equal(g6,g8)
    c: Equal(g8,g7)
    c: Symmetric(g0,g0,g-2)
    c: Equal(g0,g2)
    c: Equal(g3,g1)
FEATURE [PartDesign::SubtractiveLoft] SubtractiveLoft
  BaseFeature = -> Pocket002
  Closed = false
  Profile = -> Sketch022
  Ruled = true
  Sections = -> [Sketch025,Sketch023]
FEATURE [PartDesign::Pocket] Pocket003  label="PocketFace"
  BaseFeature = -> SubtractiveLoft
  Length = 3
  Length2 = 100
  Profile = -> Sketch024
  Reversed = true
  Type = 0
  expr: Length = <<param>>.face_thickness
FEATURE [Sketcher::SketchObject] Sketch026  label="SketchFrontScrews"
  AttachmentOffset = pos=(0,0,38) rot=(1,0,0;-0.349066rad)
  FullyConstrained = true
  MapMode = 5
  Placement = pos=(0,-38,-8.4e-15) rot=(-1,0,0;5.06145rad)
  Support = -> [XZ_Plane004]
  expr: Constraints[0] = <<param>>.front_screw_width1
  expr: Constraints[1] = <<param>>.front_screw_width2
  expr: Constraints[2] = <<param>>.front_screw_height
  expr: Constraints[13] = <<param>>.screw_hole
  expr: .AttachmentOffset.Base.z = <<param>>.mid_depth / 2 - <<param>>.face_thickness
  expr: Constraints[9] = <<param>>.face_offset + <<param>>.front_screw_offset
  expr: .AttachmentOffset.Rotation.Angle = -<<param>>.front_angle
  sketch-geometry (6):
    g0: Circle CenterX=-37 CenterY=33 CenterZ=0 NormalX=0 NormalY=0 NormalZ=1 AngleXU=0 Radius=1
    g1: Circle CenterX=37 CenterY=33 CenterZ=0 NormalX=0 NormalY=0 NormalZ=1 AngleXU=0 Radius=1
    g2: Circle CenterX=-37.75 CenterY=9 CenterZ=0 NormalX=0 NormalY=0 NormalZ=1 AngleXU=0 Radius=1
    g3: Circle CenterX=37.75 CenterY=9 CenterZ=0 NormalX=0 NormalY=0 NormalZ=1 AngleXU=0 Radius=1
    g4: LineSegment StartX=-37 StartY=33 StartZ=0 EndX=37 EndY=33 EndZ=0
    g5: LineSegment StartX=-37.75 StartY=9 StartZ=0 EndX=37.75 EndY=9 EndZ=0
  constraints (14):
    c: DistanceX(g0,g1) = 74
    c: DistanceX(g2,g3) = 75.5
    c: DistanceY(g3,g1) = 24
    c: Coincident(g4,g0)
    c: Coincident(g4,g1)
    c: Coincident(g5,g2)
    c: Coincident(g5,g3)
    c: Symmetric(g2,g3,g-2)
    c: Symmetric(g0,g1,g-2)
    c: DistanceY(g-1,g3) = 9
    c: Equal(g0,g2)
    c: Equal(g2,g3)
    c: Equal(g3,g1)
    c: Diameter(g0) = 2
FEATURE [PartDesign::Pocket] Pocket004  label="PocketFrontScrews"
  BaseFeature = -> Pocket003
  Length = 6
  Length2 = 100
  Profile = -> Sketch026
  Type = 0
FEATURE [PartDesign::Revolution] Revolution
  Angle = 360
  Axis = (-1e-16,0.309017,0.951057)
  Base = (-3.1e-15,10,24)
  BaseFeature = -> Pocket004
  Profile = -> Sketch021
  ReferenceAxis = -> Sketch021 [V_Axis]
  Reversed = true
FEATURE [PartDesign::Pocket] Pocket005  label="PocketButtonHole"
  BaseFeature = -> Revolution
  Length = 6
  Length2 = 100
  Profile = -> Sketch008
  Reversed = true
  Type = 1
FEATURE [Sketcher::SketchObject] Sketch027  label="SketchButtonCarve"
  AttachmentOffset = pos=(10,24,0) rot=(0,0,1;-0.314159rad)
  FullyConstrained = true
  MapMode = 5
  Placement = pos=(-3.1e-15,10,24) rot=(-0.506732,-0.697457,-0.506732;4.35963rad)
  Support = -> [YZ_Plane004]
  expr: .AttachmentOffset.Rotation.Angle = <<param>>.button_angle
  expr: .AttachmentOffset.Base.y = <<param>>.button_height
  expr: Constraints[6] = <<param>>.button_hole / 2 + 4
  expr: .AttachmentOffset.Base.x = <<param>>.button_offset
  expr: Constraints[12] = <<param>>.button_hole / 2 + 10
  sketch-geometry (4):
    g0: LineSegment StartX=0 StartY=2 StartZ=0 EndX=12.2 EndY=2 EndZ=0
    g1: ArcOfCircle CenterX=18.2 CenterY=3.09999 CenterZ=0 NormalX=0 NormalY=0 NormalZ=1 AngleXU=0 Radius=6.09999 StartAngle=3.32291 EndAngle=4.71239
    g2: LineSegment StartX=0 StartY=2 StartZ=0 EndX=0 EndY=-3 EndZ=0
    g3: LineSegment StartX=18.2 StartY=-3 StartZ=0 EndX=0 EndY=-3 EndZ=0
  constraints (13):
    c: Horizontal(g0)
    c: Coincident(g1,g0)
    c: Coincident(g2,g0)
    c: Coincident(g3,g1)
    c: Horizontal(g3)
    c: Tangent(g3,g1)
    c: DistanceX(g0,g0) = 12.2
    c: DistanceY(g2,g2) = 5
    c: Coincident(g2,g3)
    c: Vertical(g2)
    c: PointOnObject(g-1,g2)
    c: DistanceY(g2,g-1) = 3
    c: DistanceX(g3,g3) = 18.2
FEATURE [Sketcher::SketchObject] Sketch028  label="SketchTerminals"
  FullyConstrained = true
  MapMode = 5
  Placement = pos=(0,0,0) rot=(1,0,0;1.5708rad)
  Support = -> [XZ_Plane004]
  expr: Constraints[18] = <<param>>.terminal_thickness
  expr: Constraints[22] = <<param>>.bottom_height
  expr: Constraints[19] = <<param>>.terminal_height
  expr: Constraints[23] = <<param>>.terminal_offset
  expr: Constraints[24] = <<param>>.terminal_seperation
  sketch-geometry (15):
    g0: LineSegment StartX=10.1 StartY=-13.1 StartZ=0 EndX=10.9 EndY=-13.1 EndZ=0
    g1: LineSegment StartX=10.9 StartY=-13.1 StartZ=0 EndX=10.9 EndY=-19.5 EndZ=0
    g2: LineSegment StartX=10.9 StartY=-19.5 StartZ=0 EndX=10.1 EndY=-19.5 EndZ=0
    g3: LineSegment StartX=10.1 StartY=-19.5 StartZ=0 EndX=10.1 EndY=-13.1 EndZ=0
    g4: LineSegment StartX=-10.1 StartY=-13.1 StartZ=0 EndX=-10.9 EndY=-13.1 EndZ=0
    g5: LineSegment StartX=-10.9 StartY=-13.1 StartZ=0 EndX=-10.9 EndY=-19.5 EndZ=0
    g6: LineSegment StartX=-10.9 StartY=-19.5 StartZ=0 EndX=-10.1 EndY=-19.5 EndZ=0
    g7: LineSegment StartX=-10.1 StartY=-19.5 StartZ=0 EndX=-10.1 EndY=-13.1 EndZ=0
    g8: Circle CenterX=0 CenterY=-24 CenterZ=0 NormalX=0 NormalY=0 NormalZ=1 AngleXU=0 Radius=3
    g9: LineSegment StartX=4.5 StartY=-24 StartZ=0 EndX=11.5 EndY=-24 EndZ=0
    g10: LineSegment StartX=11.5 StartY=-24 StartZ=0 EndX=11.5 EndY=-22.2 EndZ=0
    g11: LineSegment StartX=10.5 StartY=-21.2 StartZ=0 EndX=5.5 EndY=-21.2 EndZ=0
    g12: LineSegment StartX=4.5 StartY=-22.2 StartZ=0 EndX=4.5 EndY=-24 EndZ=0
    g13: ArcOfCircle CenterX=5.5 CenterY=-22.2 CenterZ=0 NormalX=0 NormalY=0 NormalZ=1 AngleXU=0 Radius=1 StartAngle=1.5708 EndAngle=3.14159
    g14: ArcOfCircle CenterX=10.5 CenterY=-22.2 CenterZ=0 NormalX=0 NormalY=0 NormalZ=1 AngleXU=0 Radius=1 StartAngle=-9e-16 EndAngle=1.5708
  constraints (42):
    c: Coincident(g0,g1)
    c: Coincident(g1,g2)
    c: Coincident(g2,g3)
    c: Coincident(g3,g0)
    c: Horizontal(g0)
    c: Horizontal(g2)
    c: Vertical(g1)
    c: Vertical(g3)
    c: Coincident(g4,g5)
    c: Coincident(g5,g6)
    c: Coincident(g6,g7)
    c: Coincident(g7,g4)
    c: Horizontal(g4)
    c: Horizontal(g6)
    c: Vertical(g5)
    c: Vertical(g7)
    c: Equal(g7,g1)
    c: Equal(g4,g0)
    c: DistanceX(g4,g4) = 0.8
    c: DistanceY(g3,g3) = 6.4
    c: PointOnObject(g8,g-2)
    c: Radius(g8) = 3
    c: DistanceY(g8,g-1) = 24
    c: DistanceY(g8,g1) = 4.5
    c: DistanceX(g6,g1) = 21
    c: Symmetric(g4,g0,g-2)
    c: Coincident(g9,g10)
    c: Coincident(g12,g9)
    c: Horizontal(g9)
    c: Horizontal(g11)
    c: Vertical(g10)
    c: Vertical(g12)
    c: Tangent(g12,g13) = -1.5708
    c: Tangent(g11,g13) = -1.5708
    c: Tangent(g11,g14) = -1.5708
    c: Tangent(g10,g14) = -1.5708
    c: DistanceX(g9,g9) = 7
    c: DistanceY(g9,g11) = 2.8
    c: DistanceX(g8,g9) = 4.5
    c: Equal(g13,g14)
    c: Radius(g14) = 1
    c: DistanceY(g8,g9) = 0
FEATURE [Sketcher::SketchObject] Sketch029  label="SketchAccess"
  AttachmentOffset = pos=(0,0,-41) rot=(0,0,1;0rad)
  FullyConstrained = true
  MapMode = 5
  Placement = pos=(0,41,9.1e-15) rot=(1,0,0;1.5708rad)
  Support = -> [XZ_Plane004]
  expr: Constraints[16] = <<param>>.terminal_seperation - 3
  expr: Constraints[20] = <<param>>.bottom_height
  expr: Constraints[21] = <<param>>.terminal_offset + 1.5 - 0.7
  expr: .AttachmentOffset.Base.z = -<<param>>.mid_depth / 2
  sketch-geometry (9):
    g0: ArcOfCircle CenterX=-10.5 CenterY=-4.7 CenterZ=0 NormalX=0 NormalY=0 NormalZ=1 AngleXU=0 Radius=1.5 StartAngle=0 EndAngle=3.14159
    g1: ArcOfCircle CenterX=-10.5 CenterY=-18.7 CenterZ=0 NormalX=0 NormalY=0 NormalZ=1 AngleXU=0 Radius=1.5 StartAngle=3.14159 EndAngle=6.28319
    g2: LineSegment StartX=-12 StartY=-4.7 StartZ=0 EndX=-12 EndY=-18.7 EndZ=0
    g3: LineSegment StartX=-9 StartY=-4.7 StartZ=0 EndX=-9 EndY=-18.7 EndZ=0
    g4: ArcOfCircle CenterX=10.5 CenterY=-4.7 CenterZ=0 NormalX=0 NormalY=0 NormalZ=1 AngleXU=0 Radius=1.5 StartAngle=0 EndAngle=3.14159
    g5: ArcOfCircle CenterX=10.5 CenterY=-18.7 CenterZ=0 NormalX=0 NormalY=0 NormalZ=1 AngleXU=0 Radius=1.5 StartAngle=3.14159 EndAngle=6.28319
    g6: LineSegment StartX=9 StartY=-4.7 StartZ=0 EndX=9 EndY=-18.7 EndZ=0
    g7: LineSegment StartX=12 StartY=-4.7 StartZ=0 EndX=12 EndY=-18.7 EndZ=0
    g8: Circle CenterX=0 CenterY=-24 CenterZ=0 NormalX=0 NormalY=0 NormalZ=1 AngleXU=0 Radius=3
  constraints (22):
    c: Tangent(g0,g3) = 1.5708
    c: Tangent(g0,g2) = -1.5708
    c: Tangent(g2,g1) = -1.5708
    c: Tangent(g3,g1) = 1.5708
    c: Vertical(g2)
    c: Equal(g0,g1)
    c: Tangent(g4,g7) = 1.5708
    c: Tangent(g4,g6) = -1.5708
    c: Tangent(g6,g5) = -1.5708
    c: Tangent(g7,g5) = 1.5708
    c: Vertical(g6)
    c: Equal(g4,g5)
    c: DistanceX(g0,g0) = 3
    c: DistanceX(g4,g4) = 3
    c: DistanceY(g5,g4) = 14
    c: Equal(g3,g6)
    c: DistanceX(g1,g5) = 18
    c: Symmetric(g0,g4,g-2)
    c: PointOnObject(g8,g-2)
    c: Radius(g8) = 3
    c: DistanceY(g8,g-1) = 24
    c: DistanceY(g8,g5) = 5.3
FEATURE [PartDesign::Groove] Groove
  Angle = 360
  Axis = (-1e-16,0.309017,0.951057)
  Base = (-3.1e-15,10,24)
  BaseFeature = -> Pocket005
  Profile = -> Sketch027
  ReferenceAxis = -> Sketch027 [V_Axis]
FEATURE [PartDesign::Pocket] Pocket007  label="PocketTerminals"
  BaseFeature = -> Groove
  Length = 5
  Length2 = 100
  Midplane = true
  Profile = -> Sketch028
  Type = 1
FEATURE [PartDesign::Pocket] Pocket008  label="PocketAccess"
  BaseFeature = -> Pocket007
  Length = 22
  Length2 = 100
  Profile = -> Sketch029
  Reversed = true
  Type = 0
  expr: Length = <<param>>.terminal_depth
FEATURE [PartDesign::Body] Body003  label="BodyFront"
  Group = -> [Sketch017,Pad003,Boolean,Sketch018,Pocket,Sketch019,Pad004,Pocket002,Sketch008,Sketch021,Sketch022,Sketch025,Sketch023,Sketch024,Sketch,SubtractiveLoft,Pocket003,Sketch026,Pocket004,Revolution,Pocket005,Groove,Sketch027,Sketch028,Pocket007,Sketch029,Pocket008]
  Origin = -> Origin004
  Tip = -> Pocket008
FEATURE [App::Part] Part
  Group = -> [Body003]
  Origin = -> Origin
